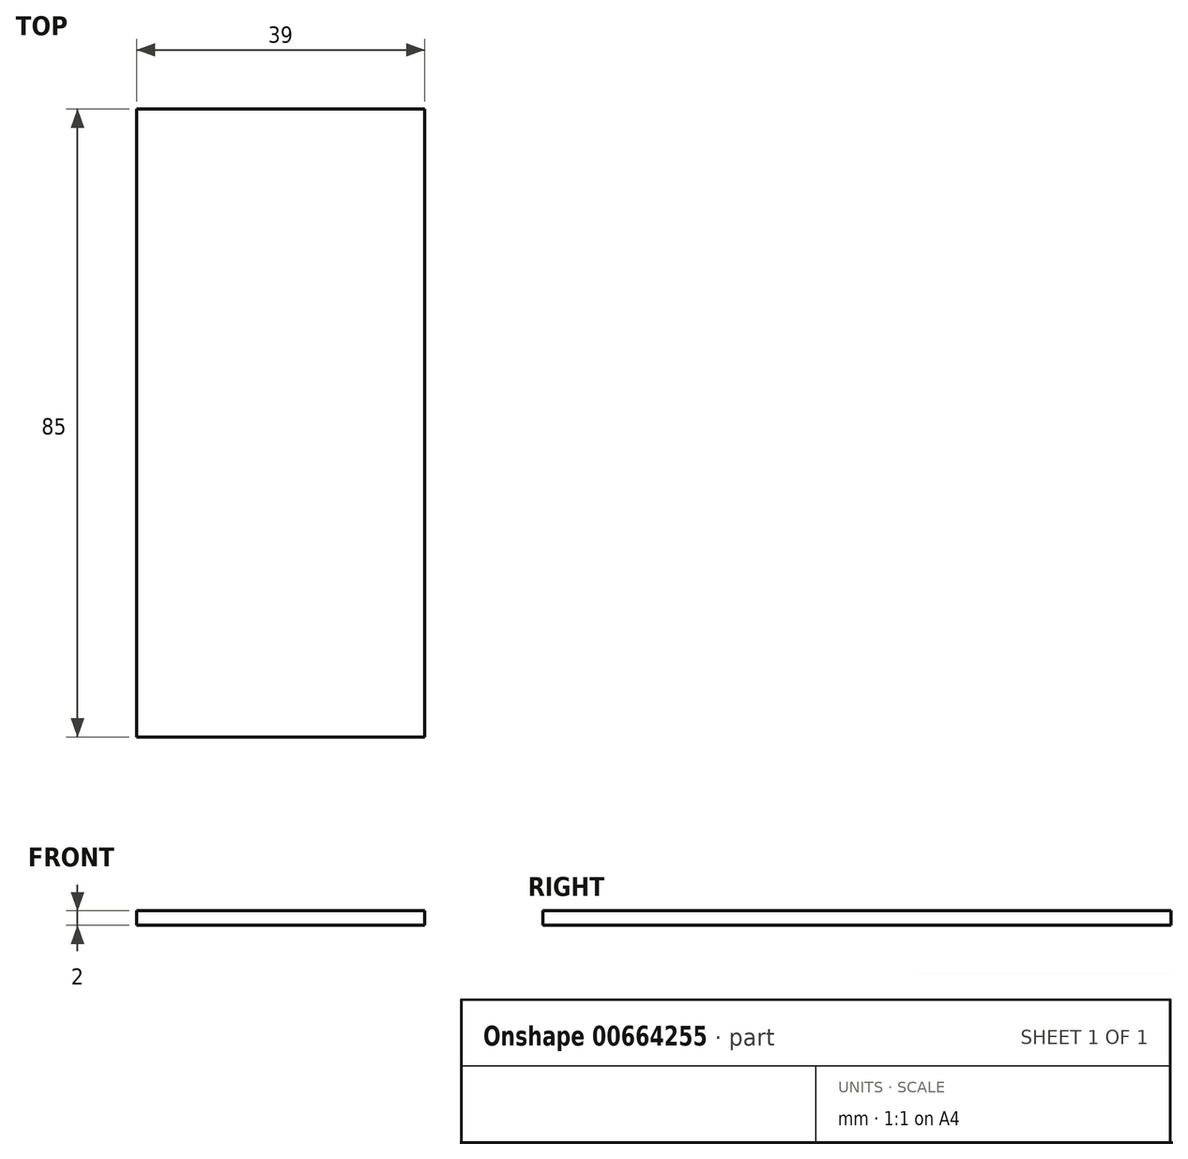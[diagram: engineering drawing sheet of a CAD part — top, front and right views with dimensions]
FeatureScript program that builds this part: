
annotation { "Feature Type Name" : "Feature", "Feature Type Description" : "" }
export const myFeature = defineFeature(function(context is Context, id is Id, definition is map)
    precondition{}
    {
        {
            var Q0;
            Q0=qCreatedBy(makeId("Front.planeOp"),FACE);
            var sketch = newSketch(context, id + "F0", { "sketchPlane" : qUnion([Q0])});
            skLineSegment(sketch, "E0.bottom", {"start": v(19.5, 1) * mm, "end": v(-19.5, 1) * mm});
            skLineSegment(sketch, "E0.top", {"start": v(19.5, -1) * mm, "end": v(-19.5, -1) * mm});
            skLineSegment(sketch, "E0.left", {"start": v(19.5, 1) * mm, "end": v(19.5, -1) * mm});
            skLineSegment(sketch, "E0.right", {"start": v(-19.5, 1) * mm, "end": v(-19.5, -1) * mm});
            skPoint(sketch, "E0.middle", {"position": v(0, 0) * mm});
            skSolve(sketch);
        }
        {
            var Q0;
            Q0=makeQuery(id+"F0.imprint","IMPRINT",FACE,{"disambiguationData":[TD([[makeQuery(id+"F0.imprint","IMPRINT",EDGE,{"derivedFrom":sQuery(id+"F0.wireOp",EDGE,"E0.bottom")}),1.0]])]});
            extrude(context, id + "F1", {"entities" : qUnion([Q0]), "depth" : 85 * mm, "offsetDistance" : 25 * mm});
        }
    });
